# Revit family: 1413 Pimlico 500
name_source: partatom
category: Lighting Fixtures
revit_build: Autodesk Revit 2018 (Build: 20170223_1515(x64)
units: mm (PartAtom-declared; Revit-internal decimal feet)

## family parameters
Always vertical = Yes
Cut with Voids When Loaded = No
Host = Wall
Light Source = No
OmniClass Number = 23.80.70.00
OmniClass Title = Lighting
Part Type = Normal
Room Calculation Point = No
Round Connector Dimension = Use Diameter
Shared = No

## types (2) — shared parameters
Driver Required = No
Manufacturer = Astro Lighting Ltd
Manufacturer URL - Europe and Rest of World = www.astrolighting.com
Manufacturer URL - North America = us.astrolighting.com
URL = www.astrolighting.com

## per-type parameters (varying)
| type | ADA compliant | Assembly Code | Dimmable | Dimming Method | Efficacy (lm/w) | Electrical Class | Lamp | Light Source Fixed | Location / IP Rating | Main Finish | Main Material | Product CCT | Product CRI | Product Dimensions (MM) | Product Location | Product Name | Product SKU | Product Weight (KG) | Wattage Comments |
| CE | N / A | OL222 | Yes | Lamp Dependent | Lamp Dependent | 1 | E27 | Replaceable | Outdoor/IP23 | Textured Black, Bronze, Antique Brass | Metal - Stainless Steel | Lamp Dependent | Lamp Dependent | 500x154x212 | Wall -Vertical | Pimlico 500 | 1413004 | 3.37 | 60W Max |
| ETL |  |  |  |  |  | 0 |  |  | DAMP |  | Metal - Steel | 2700K / 3000K | 80 / 90 |  | Bathroom |  | 1234001 |  |  |

## geometry (parser evidence)
native form markers: Sweep x2
no freeform markers — native parametric forms only
